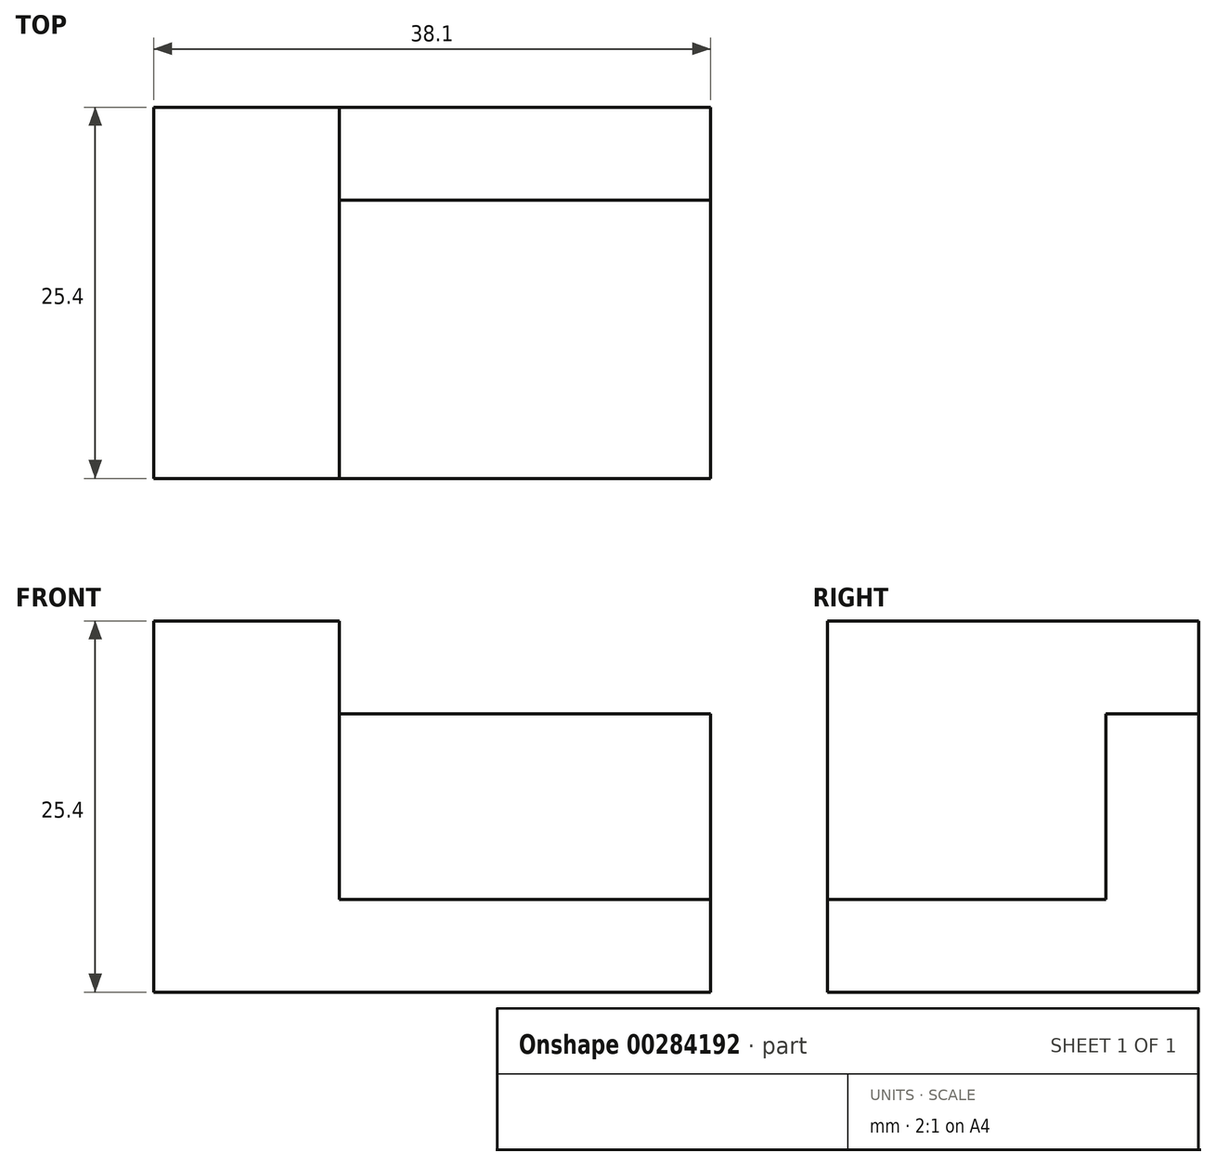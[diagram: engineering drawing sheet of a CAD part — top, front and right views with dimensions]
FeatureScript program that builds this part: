
annotation { "Feature Type Name" : "Feature", "Feature Type Description" : "" }
export const myFeature = defineFeature(function(context is Context, id is Id, definition is map)
    precondition{}
    {
        {
            var Q0;
            Q0=qCreatedBy(makeId("Front.planeOp"),FACE);
            var sketch = newSketch(context, id + "F0", { "sketchPlane" : qUnion([Q0])});
            skLineSegment(sketch, "E0", {"start": v(0, 0) * mm, "end": v(0, 25.4) * mm});
            skLineSegment(sketch, "E1", {"start": v(0, 25.4) * mm, "end": v(12.7, 25.4) * mm});
            skLineSegment(sketch, "E2", {"start": v(12.7, 25.4) * mm, "end": v(12.7, 19.05) * mm});
            skLineSegment(sketch, "E3", {"start": v(12.7, 19.05) * mm, "end": v(38.1, 19.05) * mm});
            skLineSegment(sketch, "E4", {"start": v(38.1, 19.05) * mm, "end": v(38.1, 0) * mm});
            skLineSegment(sketch, "E5", {"start": v(38.1, 0) * mm, "end": v(0, 0) * mm});
            skSolve(sketch);
        }
        {
            var Q0;
            Q0=makeQuery(id+"F0.imprint","IMPRINT",FACE,{"disambiguationData":[TD([[makeQuery(id+"F0.imprint","IMPRINT",EDGE,{"derivedFrom":sQuery(id+"F0.wireOp",EDGE,"E0")}),-1.0]])]});
            extrude(context, id + "F1", {"entities" : qUnion([Q0]), "endBound" : BoundingType.SYMMETRIC, "depth" : 25.4 * mm});
        }
        {
            var Q0;
            Q0=makeQuery(id+"F1.opExtrude","SWEPT_FACE",FACE,{"disambiguationData":[OSD([sQuery(id+"F0.wireOp",EDGE,"E4")])]});
            var sketch = newSketch(context, id + "F2", { "sketchPlane" : qUnion([Q0])});
            skLineSegment(sketch, "E6", {"start": v(6.35, 19.05) * mm, "end": v(6.35, 6.35) * mm});
            skLineSegment(sketch, "E7", {"start": v(6.35, 6.35) * mm, "end": v(-12.7, 6.35) * mm});
            skLineSegment(sketch, "E8", {"start": v(-12.7, 6.35) * mm, "end": v(-12.7, 0) * mm});
            skLineSegment(sketch, "E9", {"start": v(-12.7, 0) * mm, "end": v(12.7, 0) * mm});
            skLineSegment(sketch, "E10", {"start": v(12.7, 0) * mm, "end": v(12.7, 19.05) * mm});
            skLineSegment(sketch, "E11", {"start": v(12.7, 19.05) * mm, "end": v(6.35, 19.05) * mm});
            skSolve(sketch);
        }
        {
            var Q0;
            {var subQ0=sQuery(id+"F2.wireOp",EDGE,"E6");Q0=makeQuery(id+"F2.imprint","IMPRINT",FACE,{"disambiguationData":[TD([[makeQuery(id+"F2.imprint","IMPRINT",EDGE,{"derivedFrom":subQ0}),-1.0]])]});}
            extrude(context, id + "F3", {"entities" : qUnion([Q0]), "operationType" : NewBodyOperationType.REMOVE, "oppositeDirection" : true, "depth" : 25.4 * mm});
        }
    });
